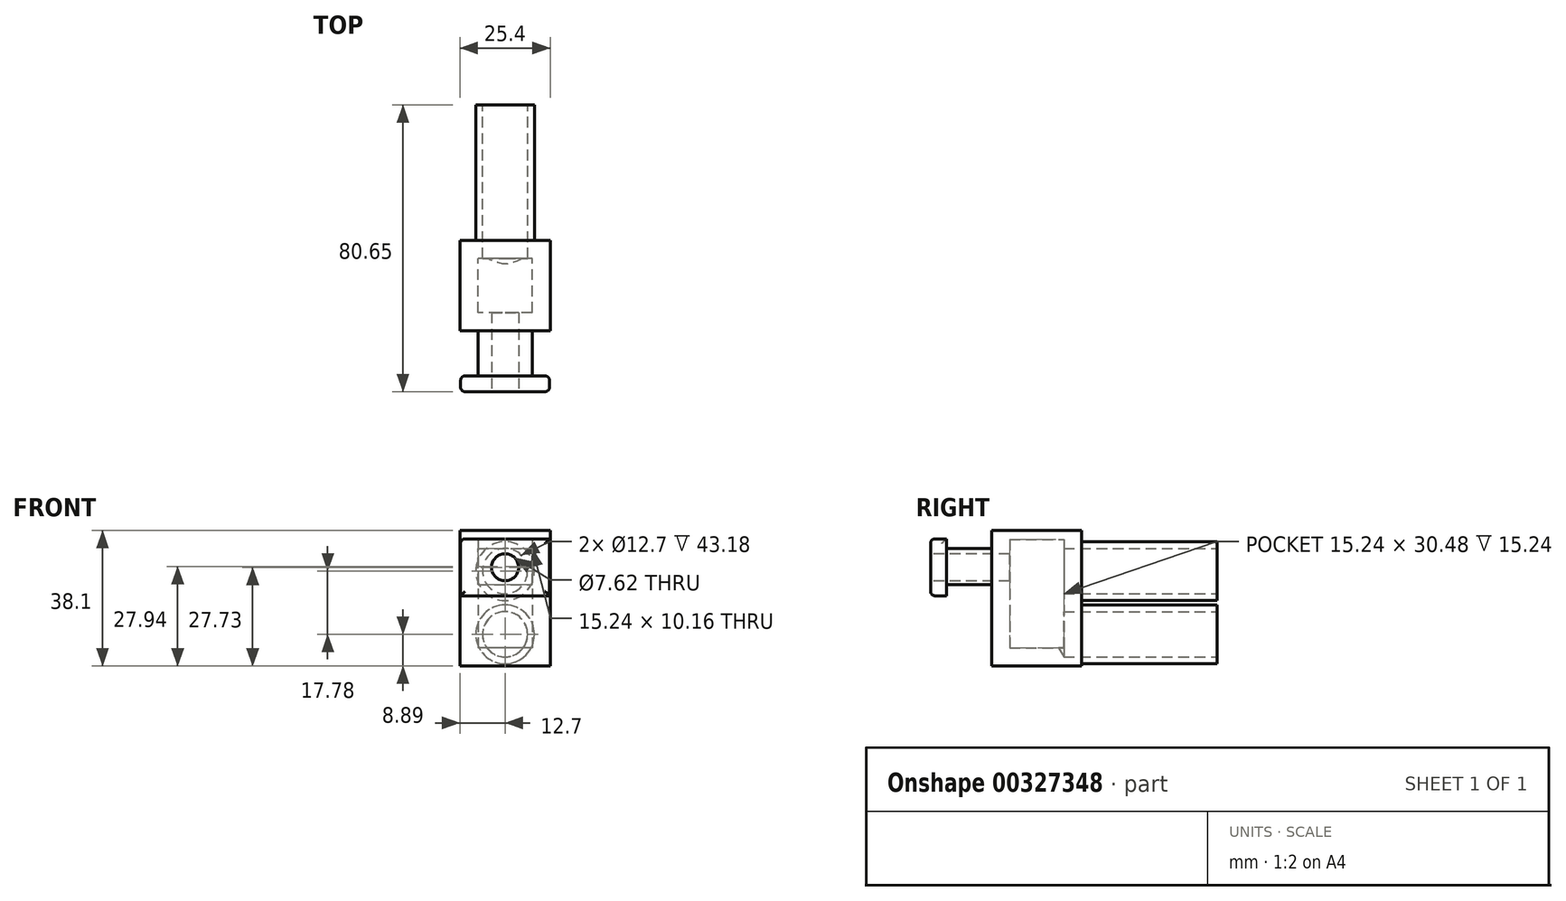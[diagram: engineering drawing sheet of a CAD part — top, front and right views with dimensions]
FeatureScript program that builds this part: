
annotation { "Feature Type Name" : "Feature", "Feature Type Description" : "" }
export const myFeature = defineFeature(function(context is Context, id is Id, definition is map)
    precondition{}
    {
        {
            var Q0;
            Q0=qCreatedBy(makeId("Top.planeOp"),FACE);
            var sketch = newSketch(context, id + "F0", { "sketchPlane" : qUnion([Q0])});
            skLineSegment(sketch, "E0.bottom", {"start": v(12.7, -12.7) * mm, "end": v(-12.7, -12.7) * mm});
            skLineSegment(sketch, "E0.top", {"start": v(12.7, 12.7) * mm, "end": v(-12.7, 12.7) * mm});
            skLineSegment(sketch, "E0.left", {"start": v(12.7, -12.7) * mm, "end": v(12.7, 12.7) * mm});
            skLineSegment(sketch, "E0.right", {"start": v(-12.7, -12.7) * mm, "end": v(-12.7, 12.7) * mm});
            skPoint(sketch, "E0.middle", {"position": v(0, 0) * mm});
            skSolve(sketch);
        }
        {
            var Q0;
            Q0 = qSketchRegion(id + "F0", true);
            extrude(context, id + "F1", {"entities" : qUnion([Q0]), "depth" : 35.56 * mm});
        }
        {
            var Q0;
            Q0=makeQuery(id+"F1.opExtrude","CAP_FACE",FACE,{"disambiguationData":[OSD([sQuery(id+"F0.wireOp",EDGE,"E0.bottom"),sQuery(id+"F0.wireOp",EDGE,"E0.top"),sQuery(id+"F0.wireOp",EDGE,"E0.left"),sQuery(id+"F0.wireOp",EDGE,"E0.right")])],"isStart":false});
            shell(context, id + "F2", {"entities" : qUnion([Q0]), "thickness" : 5.08 * mm});
        }
        {
            var Q0;
            Q0=makeQuery(id+"F1.opExtrude","CAP_FACE",FACE,{"disambiguationData":[OSD([sQuery(id+"F0.wireOp",EDGE,"E0.bottom"),sQuery(id+"F0.wireOp",EDGE,"E0.top"),sQuery(id+"F0.wireOp",EDGE,"E0.left"),sQuery(id+"F0.wireOp",EDGE,"E0.right")])],"isStart":false});
            var sketch = newSketch(context, id + "F3", { "sketchPlane" : qUnion([Q0])});
            skLineSegment(sketch, "E1.bottom", {"start": v(12.7, -12.7) * mm, "end": v(-12.7, -12.7) * mm});
            skLineSegment(sketch, "E1.top", {"start": v(12.7, 12.7) * mm, "end": v(-12.7, 12.7) * mm});
            skLineSegment(sketch, "E1.left", {"start": v(12.7, -12.7) * mm, "end": v(12.7, 12.7) * mm});
            skLineSegment(sketch, "E1.right", {"start": v(-12.7, -12.7) * mm, "end": v(-12.7, 12.7) * mm});
            skSolve(sketch);
        }
        {
            var Q0;
            Q0 = qSketchRegion(id + "F3", true);
            extrude(context, id + "F4", {"entities" : qUnion([Q0]), "operationType" : NewBodyOperationType.ADD, "depth" : 2.54 * mm});
        }
        {
            var Q0;
            Q0=makeQuery(id+"F4.boolean.opBoolean","MERGE",FACE,{"derivedFrom":[makeQuery(id+"F1.opExtrude","SWEPT_FACE",FACE,{"disambiguationData":[OSD([sQuery(id+"F0.wireOp",EDGE,"E0.top")])]}),makeQuery(id+"F4.opExtrude","SWEPT_FACE",FACE,{"disambiguationData":[OSD([sQuery(id+"F3.wireOp",EDGE,"E1.top")])]})]});
            var sketch = newSketch(context, id + "F5", { "sketchPlane" : qUnion([Q0])});
            skCircle(sketch, "E2", {"center": v(0, 26.67) * mm, "radius": 6.35 * mm});
            skCircle(sketch, "E3", {"center": v(0, 8.9) * mm, "radius": 6.35 * mm});
            skCircle(sketch, "E4", {"center": v(0, 26.67) * mm, "radius": 8.26 * mm});
            skCircle(sketch, "E5", {"center": v(0, 8.9) * mm, "radius": 8.26 * mm});
            skSolve(sketch);
        }
        {
            var Q0;
            Q0=sQuery(id+"F5.wireOp",VERTEX,"E2.center");
            var Q1;
            Q1=sQuery(id+"F5.wireOp",VERTEX,"E3.center");
            var Q2;
            Q2=makeQuery(id+"F1.opExtrude","SWEPT_BODY",BODY,{"disambiguationData":[OSD([sQuery(id+"F0.wireOp",EDGE,"E0.bottom"),sQuery(id+"F0.wireOp",EDGE,"E0.top"),sQuery(id+"F0.wireOp",EDGE,"E0.left"),sQuery(id+"F0.wireOp",EDGE,"E0.right")])]});
            hole(context, id + "F6", {"style" : HoleStyle.SIMPLE, "endStyle" : HoleEndStyle.BLIND, "holeDiameter" : 12.7 * mm, "holeDepth" : 5.08 * mm, "tappedDepth" : 12.7 * mm, "tapClearance" : 3, "locations" : qUnion([Q0, Q1]), "scope" : qUnion([Q2])});
        }
        {
            var Q0;
            Q0=makeQuery(id+"F4.boolean.opBoolean","MERGE",FACE,{"derivedFrom":[makeQuery(id+"F1.opExtrude","SWEPT_FACE",FACE,{"disambiguationData":[OSD([sQuery(id+"F0.wireOp",EDGE,"E0.bottom")])]}),makeQuery(id+"F4.opExtrude","SWEPT_FACE",FACE,{"disambiguationData":[OSD([sQuery(id+"F3.wireOp",EDGE,"E1.bottom")])]})]});
            var sketch = newSketch(context, id + "F7", { "sketchPlane" : qUnion([Q0])});
            skLineSegment(sketch, "E6.bottom", {"start": v(-7.62, 22.86) * mm, "end": v(7.62, 22.86) * mm});
            skLineSegment(sketch, "E6.top", {"start": v(-7.62, 33.02) * mm, "end": v(7.62, 33.02) * mm});
            skLineSegment(sketch, "E6.left", {"start": v(-7.62, 22.86) * mm, "end": v(-7.62, 33.02) * mm});
            skLineSegment(sketch, "E6.right", {"start": v(7.62, 22.86) * mm, "end": v(7.62, 33.02) * mm});
            skPoint(sketch, "E6.middle", {"position": v(0, 27.94) * mm});
            skSolve(sketch);
        }
        {
            var Q0;
            Q0 = qSketchRegion(id + "F7", true);
            extrude(context, id + "F8", {"entities" : qUnion([Q0]), "operationType" : NewBodyOperationType.ADD, "depth" : 12.7 * mm});
        }
        {
            var Q0;
            Q0=makeQuery(id+"F8.opExtrude","CAP_FACE",FACE,{"disambiguationData":[OSD([sQuery(id+"F7.wireOp",EDGE,"E6.bottom"),sQuery(id+"F7.wireOp",EDGE,"E6.top"),sQuery(id+"F7.wireOp",EDGE,"E6.left"),sQuery(id+"F7.wireOp",EDGE,"E6.right")])],"isStart":false});
            var sketch = newSketch(context, id + "F9", { "sketchPlane" : qUnion([Q0])});
            skLineSegment(sketch, "E7.bottom", {"start": v(5.92, 24.37) * mm, "end": v(-5.92, 24.37) * mm});
            skLineSegment(sketch, "E7.top", {"start": v(5.92, 31.09) * mm, "end": v(-5.92, 31.09) * mm});
            skLineSegment(sketch, "E7.left", {"start": v(5.92, 24.37) * mm, "end": v(5.92, 31.09) * mm});
            skLineSegment(sketch, "E7.right", {"start": v(-5.92, 24.37) * mm, "end": v(-5.92, 31.09) * mm});
            skPoint(sketch, "E7.middle", {"position": v(0, 27.73) * mm});
            skPoint(sketch, "E7.middle.positionSnap0", {"position": v(0, 33.02) * mm});
            skPoint(sketch, "E7.centerSnap0", {"position": v(0, 33.02) * mm});
            skSolve(sketch);
        }
        {
            var Q0;
            Q0=sQuery(id+"F9.wireOp",VERTEX,"E7.middle");
            var Q1;
            Q1=makeQuery(id+"F1.opExtrude","SWEPT_BODY",BODY,{"disambiguationData":[OSD([sQuery(id+"F0.wireOp",EDGE,"E0.bottom"),sQuery(id+"F0.wireOp",EDGE,"E0.top"),sQuery(id+"F0.wireOp",EDGE,"E0.left"),sQuery(id+"F0.wireOp",EDGE,"E0.right")])]});
            hole(context, id + "F10", {"style" : HoleStyle.SIMPLE, "endStyle" : HoleEndStyle.BLIND, "holeDiameter" : 7.62 * mm, "holeDepth" : 20.32 * mm, "tappedDepth" : 12.7 * mm, "tapClearance" : 3, "locations" : qUnion([Q0]), "scope" : qUnion([Q1])});
        }
        {
            var Q0;
            Q0=makeQuery(id+"F8.opExtrude","CAP_FACE",FACE,{"disambiguationData":[OSD([sQuery(id+"F7.wireOp",EDGE,"E6.bottom"),sQuery(id+"F7.wireOp",EDGE,"E6.top"),sQuery(id+"F7.wireOp",EDGE,"E6.left"),sQuery(id+"F7.wireOp",EDGE,"E6.right")])],"isStart":false});
            var sketch = newSketch(context, id + "F11", { "sketchPlane" : qUnion([Q0])});
            skLineSegment(sketch, "E8.bottom", {"start": v(-12.5, 19.73) * mm, "end": v(12.5, 19.73) * mm});
            skLineSegment(sketch, "E8.top", {"start": v(-12.5, 35.73) * mm, "end": v(12.5, 35.73) * mm});
            skLineSegment(sketch, "E8.left", {"start": v(-12.5, 19.73) * mm, "end": v(-12.5, 35.73) * mm});
            skLineSegment(sketch, "E8.right", {"start": v(12.5, 19.73) * mm, "end": v(12.5, 35.73) * mm});
            skPoint(sketch, "E8.middle", {"position": v(0, 27.73) * mm});
            skSolve(sketch);
        }
        {
            var Q0;
            Q0 = qSketchRegion(id + "F11", true);
            extrude(context, id + "F12", {"entities" : qUnion([Q0]), "operationType" : NewBodyOperationType.ADD, "depth" : 4.44 * mm});
        }
        {
            var Q0;
            Q0=makeQuery(id+"F12.opExtrude","CAP_FACE",FACE,{"disambiguationData":[OSD([sQuery(id+"F11.wireOp",EDGE,"E8.bottom"),sQuery(id+"F11.wireOp",EDGE,"E8.top"),sQuery(id+"F11.wireOp",EDGE,"E8.left"),sQuery(id+"F11.wireOp",EDGE,"E8.right")])],"isStart":false});
            var sketch = newSketch(context, id + "F13", { "sketchPlane" : qUnion([Q0])});
            skLineSegment(sketch, "E9.bottom", {"start": v(-5.92, 24.38) * mm, "end": v(5.92, 24.38) * mm});
            skLineSegment(sketch, "E9.top", {"start": v(-5.92, 31.08) * mm, "end": v(5.92, 31.08) * mm});
            skLineSegment(sketch, "E9.left", {"start": v(-5.92, 24.38) * mm, "end": v(-5.92, 31.08) * mm});
            skLineSegment(sketch, "E9.right", {"start": v(5.92, 24.38) * mm, "end": v(5.92, 31.08) * mm});
            skPoint(sketch, "E9.middle", {"position": v(0, 27.73) * mm});
            skPoint(sketch, "E9.middle.positionSnap0", {"position": v(0, 19.73) * mm});
            skPoint(sketch, "E9.middle.positionSnap1", {"position": v(-12.5, 27.73) * mm});
            skPoint(sketch, "E9.centerSnap0", {"position": v(0, 19.73) * mm});
            skPoint(sketch, "E9.centerSnap1", {"position": v(-12.5, 27.73) * mm});
            skSolve(sketch);
        }
        {
            var Q0;
            Q0=sQuery(id+"F13.wireOp",VERTEX,"E9.middle");
            var Q1;
            Q1=makeQuery(id+"F1.opExtrude","SWEPT_BODY",BODY,{"disambiguationData":[OSD([sQuery(id+"F0.wireOp",EDGE,"E0.bottom"),sQuery(id+"F0.wireOp",EDGE,"E0.top"),sQuery(id+"F0.wireOp",EDGE,"E0.left"),sQuery(id+"F0.wireOp",EDGE,"E0.right")])]});
            hole(context, id + "F14", {"style" : HoleStyle.SIMPLE, "endStyle" : HoleEndStyle.BLIND, "holeDiameter" : 7.62 * mm, "holeDepth" : 20.32 * mm, "tappedDepth" : 12.7 * mm, "tapClearance" : 3, "locations" : qUnion([Q0]), "scope" : qUnion([Q1])});
        }
        {
            var Q0;
            Q0=makeQuery(id+"F12.opExtrude","CAP_EDGE",EDGE,{"disambiguationData":[OSD([sQuery(id+"F11.wireOp",EDGE,"E8.top")])],"isStart":false});
            var Q1;
            Q1=makeQuery(id+"F12.opExtrude","SWEPT_EDGE",EDGE,{"disambiguationData":[OSD([sQuery(id+"F11.wireOp",EDGE,"E8.top"),sQuery(id+"F11.wireOp",EDGE,"E8.left")])]});
            var Q2;
            Q2=makeQuery(id+"F12.opExtrude","CAP_EDGE",EDGE,{"disambiguationData":[OSD([sQuery(id+"F11.wireOp",EDGE,"E8.left")])],"isStart":false});
            var Q3;
            Q3=makeQuery(id+"F12.opExtrude","CAP_EDGE",EDGE,{"disambiguationData":[OSD([sQuery(id+"F11.wireOp",EDGE,"E8.left")])],"isStart":true});
            var Q4;
            Q4=makeQuery(id+"F12.opExtrude","CAP_EDGE",EDGE,{"disambiguationData":[OSD([sQuery(id+"F11.wireOp",EDGE,"E8.right")])],"isStart":true});
            var Q5;
            Q5=makeQuery(id+"F12.opExtrude","CAP_EDGE",EDGE,{"disambiguationData":[OSD([sQuery(id+"F11.wireOp",EDGE,"E8.bottom")])],"isStart":false});
            var Q6;
            Q6=makeQuery(id+"F12.opExtrude","CAP_EDGE",EDGE,{"disambiguationData":[OSD([sQuery(id+"F11.wireOp",EDGE,"E8.right")])],"isStart":false});
            fillet(context, id + "F15", {"entities" : qUnion([Q0, Q1, Q2, Q3, Q4, Q5, Q6]), "radius" : 1.27 * mm, "tangentPropagation" : true, "allowEdgeOverflow" : false});
        }
        {
            var Q0;
            Q0 = qSketchRegion(id + "F5", true);
            extrude(context, id + "F16", {"entities" : qUnion([Q0]), "operationType" : NewBodyOperationType.ADD, "depth" : 38.1 * mm});
        }
    });
